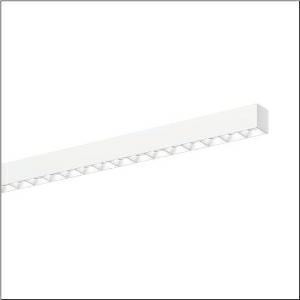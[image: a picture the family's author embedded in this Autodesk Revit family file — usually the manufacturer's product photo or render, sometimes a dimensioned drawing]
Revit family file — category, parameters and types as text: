
# Revit family: silica_r__21_51mx26da44wb_24d1
name_source: partatom
category: Lighting Fixtures
units: mm (PartAtom-declared; Revit-internal decimal feet)

## family parameters
Cut with Voids When Loaded = No
Host = Face
Light Source = No
Part Type = Normal
Room Calculation Point = No
Round Connector Dimension = Use Diameter
Shared = No

## types (1)
- --- (1 x LED, 4320 lm, 23.4 W, 4000K)
    Apparent Load = 23 VA
    CIE Flux Codes = 83 98 100 100 100
    Color Rendering = 80
    Color Temperature = 4000K
    Default Elevation = 1800 mm
    Description = Silica® 21, office luminaire, primary light control with darklight reflector, of PMMA, white, CAT 2 (L<= 3000cd/m²), light emission: direct distribution, primary light characteristic: symmetric, installation type: surface-mounted, LED, rated luminous flux: 4.320lm, luminous efficacy: 185lm/W, light colour: 840, colour temperature: 4000K, control gear: DALI 2, with terminal, 3+2-pole, max. 2.5mm², mains connection: 220..240V, AC, 50/60Hz, rated input power: 23.4W, luminaire housing, of aluminium, traffic white (RAL 9016), length: 1.204mm, width: 53mm, height: 53mm, protection rating (complete): IP20, insulation class (complete): insulation class I (protective earthing), certification: CE, permissible operating ambient temperature: 0..+35°C, standard: EN 50419, packaging unit: 1 piece
    Height = 53 mm
    Lamp = 1 x LED
    Lamp Light Flux = 4320 lm
    Lamp Power = 23.4 W
    Lamp count = 1
    Length = 1204 mm
    Luminous efficacy = 185 lm/W
    Manufacturer = Siteco
    ModVariant = No
    Model = 51MX26DA44WB
    Mounting Place = Ceiling
    Mounting Type = Surface mounted
    Number of Poles = 1
    OnlyDefault = Yes
    Power Factor = 1
    Product Name = Silica® 21
    Product group = office luminaire | ceiling mounted
    ProductGroupID = 302
    Protection Class = Protection class I
    Protection Degree = IP 20
    RLX_Detail_Level = 1
    RLX_Emergency_Light_Flux = 0 lm
    RLX_Emergency_Type = 0
    RLX_Emergency_Type_DB = No
    RlxData = <blob elided: 38673 chars, md5=1d979572>
    Socket = socket
    Standby Power = 0 W
    System Light Flux = 4320 lm
    System Power = 23 W
    Type Comments = factory setting: luminous flux: 100 % | dim-lin: 254 | 337 mA
    Type Image = l_1335934.jpg
    URL = http://relux.com
    VarID = @adj_008541
    Voltage = 0 V
    Weight = 0.00 kg
    Width = 53 mm

## geometry (parser evidence)
native form markers: Blend x4, Sweep x9
no freeform markers — native parametric forms only
